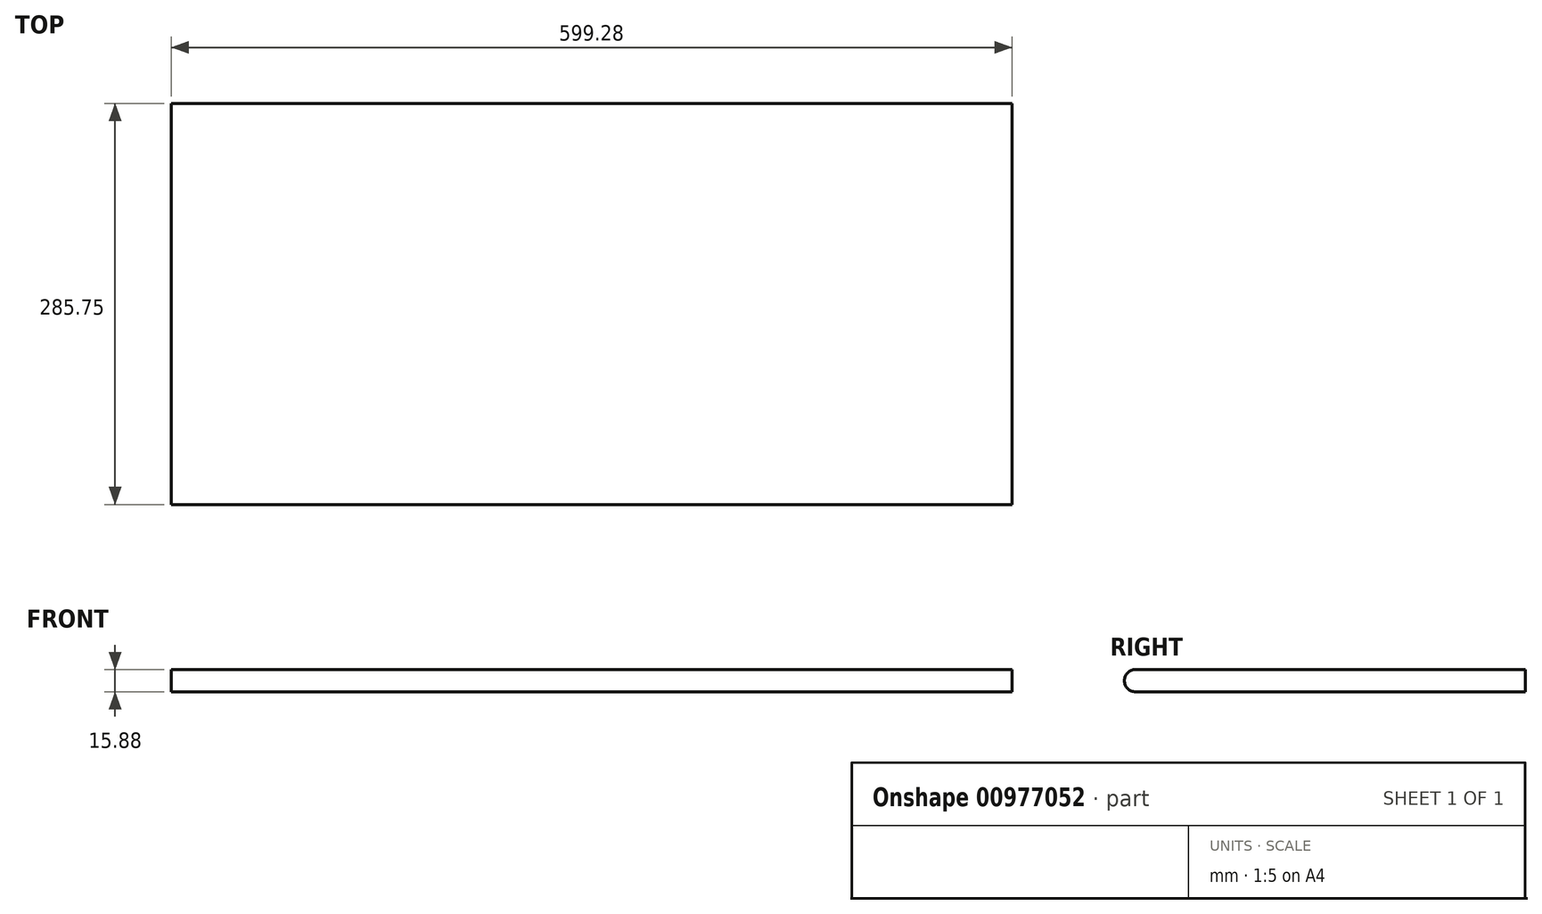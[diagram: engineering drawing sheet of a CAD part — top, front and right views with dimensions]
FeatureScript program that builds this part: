
annotation { "Feature Type Name" : "Feature", "Feature Type Description" : "" }
export const myFeature = defineFeature(function(context is Context, id is Id, definition is map)
    precondition{}
    {
        {
            var Q0;
            Q0=qCreatedBy(makeId("Right.planeOp"),FACE);
            var sketch = newSketch(context, id + "F0", { "sketchPlane" : qUnion([Q0])});
            skLineSegment(sketch, "E0.bottom", {"start": v(0, 0) * mm, "end": v(-277.81, 0) * mm});
            skLineSegment(sketch, "E0.top", {"start": v(0, -15.88) * mm, "end": v(-277.81, -15.88) * mm});
            skLineSegment(sketch, "E0.left", {"start": v(0, 0) * mm, "end": v(0, -15.88) * mm});
            skArc(sketch, "E1", {"start": v(-277.81, 0) * mm, "mid": v(-285.75, -7.94) * mm, "end": v(-277.81, -15.88) * mm});
            skSolve(sketch);
        }
        {
            var Q0;
            Q0 = qSketchRegion(id + "F0", true);
            extrude(context, id + "F1", {"entities" : qUnion([Q0]), "endBound" : BoundingType.SYMMETRIC, "depth" : 599.3 * mm, "offsetDistance" : 25.4 * mm});
        }
    });
